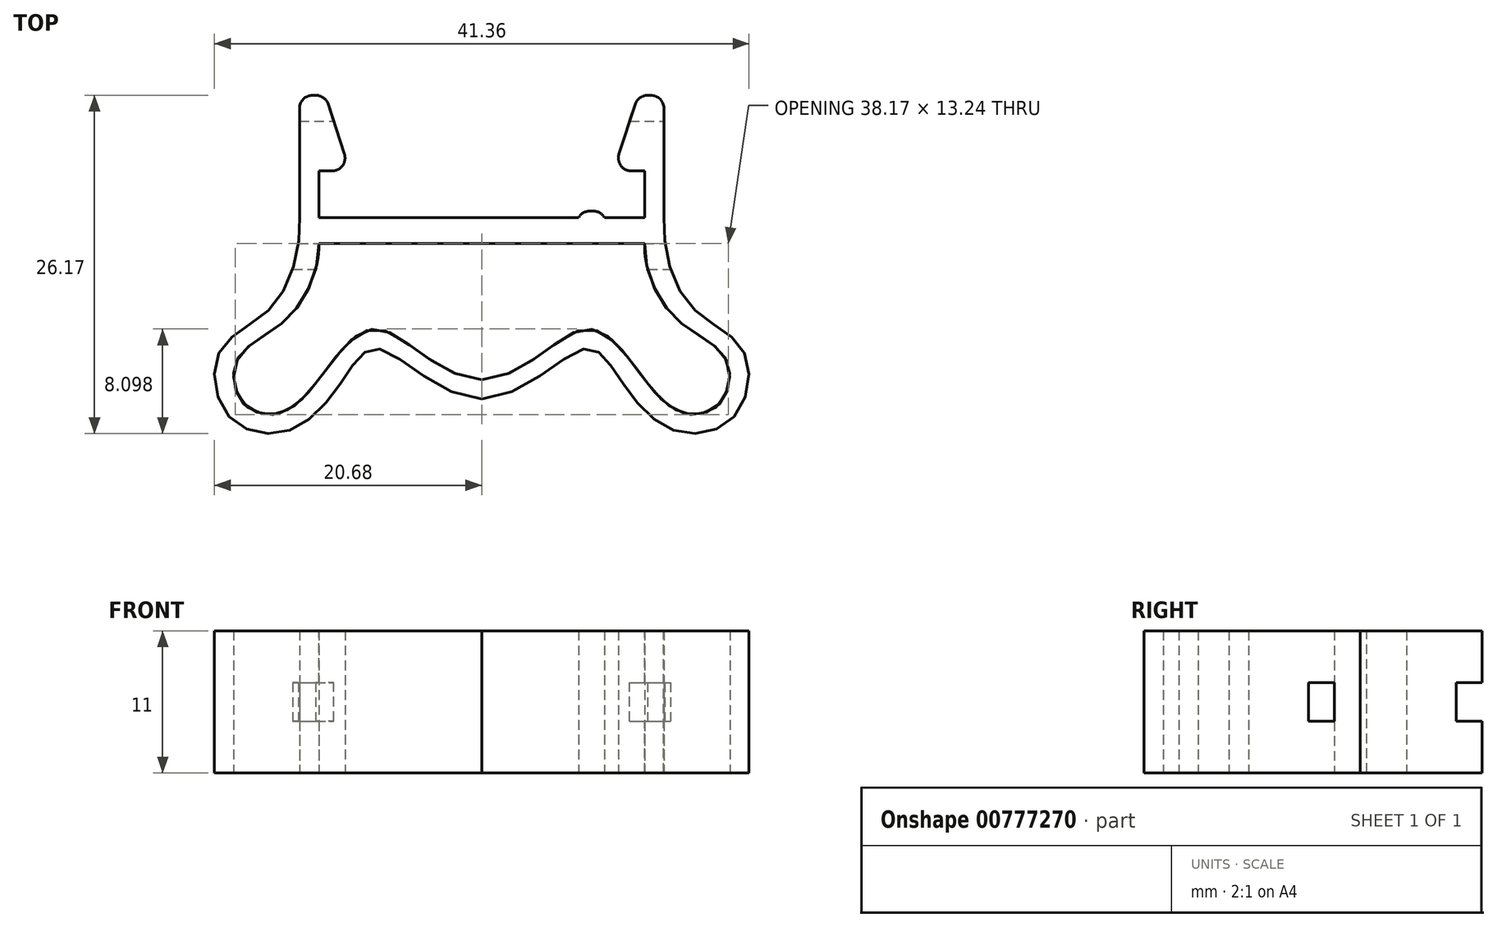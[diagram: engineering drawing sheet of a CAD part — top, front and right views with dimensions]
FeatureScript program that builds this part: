
annotation { "Feature Type Name" : "Feature", "Feature Type Description" : "" }
export const myFeature = defineFeature(function(context is Context, id is Id, definition is map)
    precondition{}
    {
        {
            var Q0;
            Q0=qCreatedBy(makeId("Top.planeOp"),FACE);
            var sketch = newSketch(context, id + "F0", { "sketchPlane" : qUnion([Q0])});
            skLineSegment(sketch, "E0", {"start": v(-14.1, 0) * mm, "end": v(-14.1, 9.45) * mm});
            skLineSegment(sketch, "E1", {"start": v(-14.1, 9.45) * mm, "end": v(-12.1, 9.45) * mm});
            skLineSegment(sketch, "E2", {"start": v(-12.1, 9.45) * mm, "end": v(-10.2, 3.6) * mm});
            skLineSegment(sketch, "E3", {"start": v(-10.2, 3.6) * mm, "end": v(-12.6, 3.6) * mm});
            skLineSegment(sketch, "E4", {"start": v(-12.6, 3.6) * mm, "end": v(-12.6, 0) * mm});
            skLineSegment(sketch, "E5", {"start": v(-12.6, 0) * mm, "end": v(0, 0) * mm});
            skLineSegment(sketch, "E6.MirrorCS", {"start": v(12.6, 0) * mm, "end": v(0, 0) * mm});
            skLineSegment(sketch, "E7.MirrorCS", {"start": v(12.6, 3.6) * mm, "end": v(12.6, 0) * mm});
            skLineSegment(sketch, "E8.MirrorCS", {"start": v(10.2, 3.6) * mm, "end": v(12.6, 3.6) * mm});
            skLineSegment(sketch, "E9.MirrorCS", {"start": v(12.1, 9.45) * mm, "end": v(10.2, 3.6) * mm});
            skLineSegment(sketch, "E10.MirrorCS", {"start": v(14.1, 9.45) * mm, "end": v(12.1, 9.45) * mm});
            skLineSegment(sketch, "E11.MirrorCS", {"start": v(14.1, 0) * mm, "end": v(14.1, 9.45) * mm});
            skLineSegment(sketch, "E12", {"start": v(-12.6, -2) * mm, "end": v(12.6, -2) * mm});
            skLineSegment(sketch, "E13.bottom", {"start": v(-9.5, 0) * mm, "end": v(-7.5, 0) * mm});
            skLineSegment(sketch, "E13.top", {"start": v(-9.5, 0.5) * mm, "end": v(-7.5, 0.5) * mm});
            skLineSegment(sketch, "E13.left", {"start": v(-9.5, 0) * mm, "end": v(-9.5, 0.5) * mm});
            skLineSegment(sketch, "E13.right", {"start": v(-7.5, 0) * mm, "end": v(-7.5, 0.5) * mm});
            skLineSegment(sketch, "E14.MirrorCS", {"start": v(9.5, 0) * mm, "end": v(9.5, 0.5) * mm});
            skLineSegment(sketch, "E15.MirrorCS", {"start": v(9.5, 0.5) * mm, "end": v(7.5, 0.5) * mm});
            skLineSegment(sketch, "E16.MirrorCS", {"start": v(7.5, 0) * mm, "end": v(7.5, 0.5) * mm});
            skFitSpline(sketch, "E17", {"points": [v(-14.1, 0) * mm, v(-16.04, -6.7) * mm, v(-20.24, -10.3) * mm, v(-19.54, -15.4) * mm, v(-14.8, -16.44) * mm, v(-10.58, -12.32) * mm, v(-8.04, -10.16) * mm, v(0, -14.04) * mm], "startDerivative": vector(2.53, -37.02) * mm, "endDerivative": vector(55.33, -0.43) * mm});
            skFitSpline(sketch, "E18", {"points": [v(-12.6, -2) * mm, v(-15.03, -7.8) * mm, v(-18.86, -10.88) * mm, v(-18.5, -14.3) * mm, v(-15.47, -15.1) * mm, v(-11.84, -11.5) * mm, v(-7.93, -8.66) * mm, v(0, -12.54) * mm], "startDerivative": vector(0.78, -38.66) * mm, "endDerivative": vector(51.1, -0.45) * mm});
            skFitSpline(sketch, "E19.MirrorCS", {"points": [v(12.6, -2) * mm, v(15.03, -7.8) * mm, v(18.86, -10.88) * mm, v(18.5, -14.3) * mm, v(15.47, -15.1) * mm, v(11.84, -11.5) * mm, v(7.93, -8.66) * mm, v(0, -12.54) * mm], "startDerivative": vector(-0.78, -38.66) * mm, "endDerivative": vector(-51.1, -0.45) * mm});
            skFitSpline(sketch, "E20.MirrorCS", {"points": [v(14.1, 0) * mm, v(16.04, -6.7) * mm, v(20.24, -10.3) * mm, v(19.54, -15.4) * mm, v(14.8, -16.44) * mm, v(10.58, -12.32) * mm, v(8.04, -10.16) * mm, v(0, -14.04) * mm], "startDerivative": vector(-2.53, -37.02) * mm, "endDerivative": vector(-55.33, -0.43) * mm});
            skSolve(sketch);
        }
        {
            var Q0;
            Q0=makeQuery(id+"F0.imprint","IMPRINT",FACE,{"disambiguationData":[TD([[makeQuery(id+"F0.imprint","IMPRINT",EDGE,{"derivedFrom":sQuery(id+"F0.wireOp",EDGE,"E0")}),-1.0]])]});
            var Q1;
            Q1=makeQuery(id+"F0.imprint","IMPRINT",FACE,{"disambiguationData":[TD([[makeQuery(id+"F0.imprint","IMPRINT",EDGE,{"derivedFrom":sQuery(id+"F0.wireOp",EDGE,"E13.bottom")}),1.0]])]});
            var Q2;
            {var subQ0=sQuery(id+"F0.wireOp",EDGE,"E14.MirrorCS");Q2=makeQuery(id+"F0.imprint","IMPRINT",FACE,{"disambiguationData":[TD([[makeQuery(id+"F0.imprint","IMPRINT",EDGE,{"derivedFrom":subQ0}),1.0]])]});}
            extrude(context, id + "F1", {"entities" : qUnion([Q0, Q1, Q2]), "depth" : 11 * mm, "offsetDistance" : 25 * mm});
        }
        {
            var Q0;
            Q0=makeQuery(id+"F1.opExtrude","SWEPT_EDGE",EDGE,{"disambiguationData":[OSD([sQuery(id+"F0.wireOp",EDGE,"E2"),sQuery(id+"F0.wireOp",EDGE,"E3")])]});
            var Q1;
            Q1=makeQuery(id+"F1.opExtrude","SWEPT_EDGE",EDGE,{"disambiguationData":[OSD([sQuery(id+"F0.wireOp",EDGE,"E0"),sQuery(id+"F0.wireOp",EDGE,"E1")])]});
            var Q2;
            Q2=makeQuery(id+"F1.opExtrude","SWEPT_EDGE",EDGE,{"disambiguationData":[OSD([sQuery(id+"F0.wireOp",EDGE,"E1"),sQuery(id+"F0.wireOp",EDGE,"E2")])]});
            var Q3;
            Q3=makeQuery(id+"F1.opExtrude","SWEPT_EDGE",EDGE,{"disambiguationData":[OSD([sQuery(id+"F0.wireOp",EDGE,"E13.top"),sQuery(id+"F0.wireOp",EDGE,"E13.left")])]});
            var Q4;
            Q4=makeQuery(id+"F1.opExtrude","SWEPT_EDGE",EDGE,{"disambiguationData":[OSD([sQuery(id+"F0.wireOp",EDGE,"E13.top"),sQuery(id+"F0.wireOp",EDGE,"E13.right")])]});
            var Q5;
            Q5=makeQuery(id+"F1.opExtrude","SWEPT_EDGE",EDGE,{"disambiguationData":[OSD([sQuery(id+"F0.wireOp",EDGE,"E15.MirrorCS"),sQuery(id+"F0.wireOp",EDGE,"E16.MirrorCS")])]});
            var Q6;
            Q6=makeQuery(id+"F1.opExtrude","SWEPT_EDGE",EDGE,{"disambiguationData":[OSD([sQuery(id+"F0.wireOp",EDGE,"E14.MirrorCS"),sQuery(id+"F0.wireOp",EDGE,"E15.MirrorCS")])]});
            var Q7;
            Q7=makeQuery(id+"F1.opExtrude","SWEPT_EDGE",EDGE,{"disambiguationData":[OSD([sQuery(id+"F0.wireOp",EDGE,"E8.MirrorCS"),sQuery(id+"F0.wireOp",EDGE,"E9.MirrorCS")])]});
            var Q8;
            Q8=makeQuery(id+"F1.opExtrude","SWEPT_EDGE",EDGE,{"disambiguationData":[OSD([sQuery(id+"F0.wireOp",EDGE,"E9.MirrorCS"),sQuery(id+"F0.wireOp",EDGE,"E10.MirrorCS")])]});
            var Q9;
            Q9=makeQuery(id+"F1.opExtrude","SWEPT_EDGE",EDGE,{"disambiguationData":[OSD([sQuery(id+"F0.wireOp",EDGE,"E10.MirrorCS"),sQuery(id+"F0.wireOp",EDGE,"E11.MirrorCS")])]});
            fillet(context, id + "F2", {"entities" : qUnion([Q0, Q1, Q2, Q3, Q4, Q5, Q6, Q7, Q8, Q9]), "radius" : 1 * mm, "tangentPropagation" : true, "allowEdgeOverflow" : false});
        }
        {
            var Q0;
            Q0=qCreatedBy(makeId("Right.planeOp"),FACE);
            var sketch = newSketch(context, id + "F3", { "sketchPlane" : qUnion([Q0])});
            skLineSegment(sketch, "E21.bottom", {"start": v(-4, 4) * mm, "end": v(-2, 4) * mm});
            skLineSegment(sketch, "E21.top", {"start": v(-4, 7) * mm, "end": v(-2, 7) * mm});
            skLineSegment(sketch, "E21.left", {"start": v(-4, 4) * mm, "end": v(-4, 7) * mm});
            skLineSegment(sketch, "E21.right", {"start": v(-2, 4) * mm, "end": v(-2, 7) * mm});
            skPoint(sketch, "E21.middle", {"position": v(-3, 5.5) * mm});
            skLineSegment(sketch, "E22.bottom", {"start": v(7.45, 4) * mm, "end": v(9.45, 4) * mm});
            skLineSegment(sketch, "E22.top", {"start": v(7.45, 7) * mm, "end": v(9.45, 7) * mm});
            skLineSegment(sketch, "E22.left", {"start": v(7.45, 4) * mm, "end": v(7.45, 7) * mm});
            skLineSegment(sketch, "E22.right", {"start": v(9.45, 4) * mm, "end": v(9.45, 7) * mm});
            skPoint(sketch, "E22.middle", {"position": v(8.45, 5.5) * mm});
            skSolve(sketch);
        }
        {
            var Q0;
            Q0=qSketchRegion(id+"F3",true);
            extrude(context, id + "F4", {"entities" : qUnion([Q0]), "operationType" : NewBodyOperationType.REMOVE, "endBound" : BoundingType.SYMMETRIC, "oppositeDirection" : true, "depth" : 30 * mm, "offsetDistance" : 25 * mm});
        }
    });
